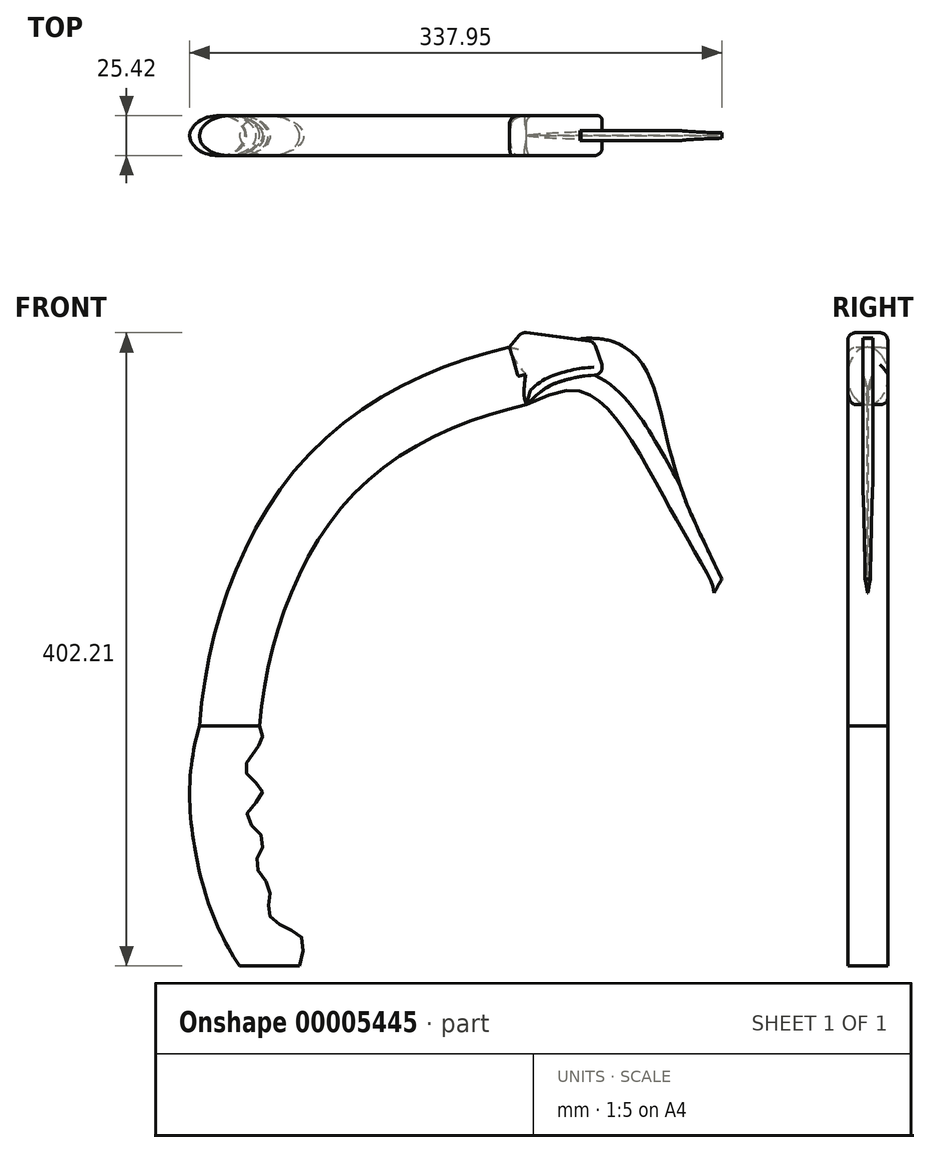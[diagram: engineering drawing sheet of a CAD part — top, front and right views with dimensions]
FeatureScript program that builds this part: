
annotation { "Feature Type Name" : "Feature", "Feature Type Description" : "" }
export const myFeature = defineFeature(function(context is Context, id is Id, definition is map)
    precondition{}
    {
        {
            var Q0;
            Q0=qCreatedBy(makeId("Top.planeOp"),FACE);
            var sketch = newSketch(context, id + "F0", { "sketchPlane" : qUnion([Q0])});
            skEllipse(sketch, "E0", {"center": v(0, 0) * mm, "majorRadius": 19.05 * mm, "minorRadius": 12.7 * mm, "majorAxis": v(-1, 0.02)});
            skLineSegment(sketch, "E1", {"start": v(0, 0) * mm, "end": v(-19.04, 0) * mm, "construction": true});
            skLineSegment(sketch, "E2", {"start": v(0, 0) * mm, "end": v(19.04, 0) * mm, "construction": true});
            skSolve(sketch);
        }
        {
            var Q0;
            Q0=qCreatedBy(makeId("Top.planeOp"),FACE);
            cPlane(context, id + "F1", {"entities" : qUnion([Q0]), "cplaneType" : CPlaneType.OFFSET, "offset" : 152.4 * mm, "width" : 152.4 * mm, "height" : 152.4 * mm});
        }
        {
            var Q0;
            Q0=qCreatedBy(id+"F1.planeOp",FACE);
            var sketch = newSketch(context, id + "F2", { "sketchPlane" : qUnion([Q0])});
            skEllipse(sketch, "E3", {"center": v(-25.4, 0) * mm, "majorRadius": 19.05 * mm, "minorRadius": 12.7 * mm, "majorAxis": v(-1, -0.03)});
            skLineSegment(sketch, "E4", {"start": v(-25.4, 0) * mm, "end": v(-44.44, 0) * mm, "construction": true});
            skLineSegment(sketch, "E5", {"start": v(-25.4, 0) * mm, "end": v(-6.36, 0) * mm, "construction": true});
            skSolve(sketch);
        }
        {
            var Q0;
            Q0=qCreatedBy(makeId("Front.planeOp"),FACE);
            var sketch = newSketch(context, id + "F3", { "sketchPlane" : qUnion([Q0])});
            skFitSpline(sketch, "E6", {"points": [v(-19.04, 0) * mm, v(-47.63, 75.12) * mm, v(-44.44, 152.4) * mm], "startDerivative": vector(-95.5, 140.87) * mm, "endDerivative": vector(49.4, 163.1) * mm});
            skFitSpline(sketch, "E7", {"points": [v(19.04, 0) * mm, v(19.67, 19.02) * mm, v(0, 31.78) * mm, v(0, 48.7) * mm, v(-8.8, 65.02) * mm, v(-3.57, 79.8) * mm, v(-14.65, 95.18) * mm, v(-4.5, 110.26) * mm, v(-15.27, 123.8) * mm, v(-6.96, 139.81) * mm, v(-6.36, 152.4) * mm], "startDerivative": vector(53.2, 280.33) * mm, "endDerivative": vector(-108.4, 99.62) * mm});
            skSolve(sketch);
        }
        {
            var Q0;
            Q0=makeQuery(id+"F2.imprint","IMPRINT",FACE,{"disambiguationData":[TD([[makeQuery(id+"F2.imprint","IMPRINT",EDGE,{"derivedFrom":sQuery(id+"F2.wireOp",EDGE,"E3")}),1.0]])]});
            var Q1;
            Q1=makeQuery(id+"F0.imprint","IMPRINT",FACE,{"disambiguationData":[TD([[makeQuery(id+"F0.imprint","IMPRINT",EDGE,{"derivedFrom":sQuery(id+"F0.wireOp",EDGE,"E0")}),1.0]])]});
            var Q2;
            Q2=sQuery(id+"F3.wireOp",EDGE,"E6");
            var Q3;
            Q3=sQuery(id+"F3.wireOp",EDGE,"E7");
            loft(context, id + "F4", {"addGuides" : true, "sheetProfilesArray" : [{ "sheetProfileEntities" : qUnion([Q0]) }, { "sheetProfileEntities" : qUnion([Q1]) }], "guidesArray" : [{ "guideEntities" : qUnion([Q2]), "guideDerivativeType" : LoftGuideDerivativeType.DEFAULT, "guideDerivativeMagnitude" : 1 }, { "guideEntities" : qUnion([Q3]), "guideDerivativeType" : LoftGuideDerivativeType.DEFAULT, "guideDerivativeMagnitude" : 1 }]});
        }
        {
            var Q0;
            Q0=qCreatedBy(makeId("Front.planeOp"),FACE);
            var sketch = newSketch(context, id + "F5", { "sketchPlane" : qUnion([Q0])});
            skFitSpline(sketch, "E8", {"points": [v(-44.44, 152.4) * mm, v(23.01, 322.86) * mm, v(152.4, 392.96) * mm], "startDerivative": vector(23.52, 350.72) * mm, "endDerivative": vector(281.64, 63.12) * mm});
            skLineSegment(sketch, "E9", {"start": v(0, 0) * mm, "end": v(152.4, 0) * mm});
            skSolve(sketch);
        }
        {
            var Q0;
            Q0=makeQuery(id+"F4.opLoft","CAP_FACE",FACE,{"disambiguationData":[OSD([makeQuery(id+"F2.imprint","IMPRINT",FACE,{"disambiguationData":[TD([[makeQuery(id+"F2.imprint","IMPRINT",EDGE,{"derivedFrom":sQuery(id+"F2.wireOp",EDGE,"E3")}),1.0]])]})])],"isStart":true});
            var Q1;
            Q1=sQuery(id+"F5.wireOp",EDGE,"E8");
            sweep(context, id + "F6", {"operationType" : NewBodyOperationType.ADD, "profiles" : qUnion([Q0]), "path" : qUnion([Q1])});
        }
        {
            var Q0;
            Q0=qCreatedBy(makeId("Front.planeOp"),FACE);
            var sketch = newSketch(context, id + "F7", { "sketchPlane" : qUnion([Q0])});
            skFitSpline(sketch, "E10", {"points": [v(197.62, 398.4) * mm, v(236.29, 382.89) * mm, v(251.85, 337) * mm, v(261.11, 304.05) * mm, v(287.2, 245.73) * mm], "startDerivative": vector(230.2, 21.85) * mm, "endDerivative": vector(193.51, -403.47) * mm});
            skFitSpline(sketch, "E11", {"points": [v(163.2, 356.44) * mm, v(207.45, 360.06) * mm, v(227.94, 336.77) * mm, v(252.58, 293.78) * mm, v(267.92, 266.78) * mm, v(280.46, 244.2) * mm, v(282.32, 236.95) * mm], "startDerivative": vector(375.19, 192.04) * mm, "endDerivative": vector(9.77, -124.3) * mm});
            skLineSegment(sketch, "E12", {"start": v(287.2, 245.73) * mm, "end": v(282.32, 236.95) * mm});
            skLineSegment(sketch, "E13", {"start": v(197.62, 398.4) * mm, "end": v(163.2, 356.44) * mm});
            skSolve(sketch);
        }
        {
            var Q0;
            Q0=makeQuery(id+"F7.imprint","IMPRINT",FACE,{"disambiguationData":[TD([[makeQuery(id+"F7.imprint","IMPRINT",EDGE,{"derivedFrom":sQuery(id+"F7.wireOp",EDGE,"E10")}),-1.0]])]});
            extrude(context, id + "F8", {"entities" : qUnion([Q0]), "operationType" : NewBodyOperationType.ADD, "endBound" : BoundingType.SYMMETRIC, "depth" : 6.35 * mm});
        }
        {
            var Q0;
            Q0=qCreatedBy(makeId("Front.planeOp"),FACE);
            var sketch = newSketch(context, id + "F9", { "sketchPlane" : qUnion([Q0])});
            skLineSegment(sketch, "E14", {"start": v(163.2, 356.44) * mm, "end": v(152.4, 392.96) * mm});
            skLineSegment(sketch, "E15", {"start": v(205.84, 396.62) * mm, "end": v(213.34, 375.23) * mm});
            skLineSegment(sketch, "E16", {"start": v(152.4, 392.96) * mm, "end": v(160.2, 402.53) * mm});
            skLineSegment(sketch, "E17", {"start": v(160.2, 402.53) * mm, "end": v(205.84, 396.62) * mm});
            skFitSpline(sketch, "E18", {"points": [v(213.34, 375.23) * mm, v(184.24, 371.01) * mm, v(163.2, 356.44) * mm], "startDerivative": vector(-74.46, 3.6) * mm, "endDerivative": vector(-65.74, -66.24) * mm});
            skSolve(sketch);
        }
        {
            var Q0;
            Q0=makeQuery(id+"F9.imprint","IMPRINT",FACE,{"disambiguationData":[TD([[makeQuery(id+"F9.imprint","IMPRINT",EDGE,{"derivedFrom":sQuery(id+"F9.wireOp",EDGE,"E14")}),-1.0]])]});
            extrude(context, id + "F10", {"entities" : qUnion([Q0]), "operationType" : NewBodyOperationType.ADD, "endBound" : BoundingType.SYMMETRIC, "depth" : 25.4 * mm});
        }
        {
            var Q0;
            Q0=makeQuery(id+"F10.opExtrude","CAP_EDGE",EDGE,{"disambiguationData":[OSD([sQuery(id+"F9.wireOp",EDGE,"E18")])],"isStart":false});
            var Q1;
            Q1=makeQuery(id+"F10.opExtrude","CAP_EDGE",EDGE,{"disambiguationData":[OSD([sQuery(id+"F9.wireOp",EDGE,"E15")])],"isStart":false});
            var Q2;
            Q2=makeQuery(id+"F10.opExtrude","CAP_EDGE",EDGE,{"disambiguationData":[OSD([sQuery(id+"F9.wireOp",EDGE,"E17")])],"isStart":false});
            var Q3;
            Q3=makeQuery(id+"F10.opExtrude","CAP_EDGE",EDGE,{"disambiguationData":[OSD([sQuery(id+"F9.wireOp",EDGE,"E16")])],"isStart":false});
            var Q4;
            {var subQ0=sQuery(id+"F9.wireOp",EDGE,"E14");var subQ1=sQuery(id+"F9.wireOp",EDGE,"E18");Q4=makeQuery(id+"F10.boolean.opBoolean","SPLIT",EDGE,{"disambiguationData":[TD([makeQuery(id+"F10.opExtrude","SWEPT_FACE",FACE,{"disambiguationData":[OSD([subQ1])]})])],"derivedFrom":makeQuery(id+"F10.opExtrude","CAP_EDGE",EDGE,{"disambiguationData":[OSD([subQ0])],"isStart":false})});}
            var Q5;
            Q5=makeQuery(id+"F10.opExtrude","SWEPT_EDGE",EDGE,{"disambiguationData":[OSD([sQuery(id+"F9.wireOp",EDGE,"E16"),sQuery(id+"F9.wireOp",EDGE,"E17")])]});
            var Q6;
            Q6=makeQuery(id+"F10.opExtrude","CAP_EDGE",EDGE,{"disambiguationData":[OSD([sQuery(id+"F9.wireOp",EDGE,"E16")])],"isStart":true});
            var Q7;
            {var subQ0=sQuery(id+"F9.wireOp",EDGE,"E14");var subQ1=sQuery(id+"F9.wireOp",EDGE,"E16");Q7=makeQuery(id+"F10.boolean.opBoolean","SPLIT",EDGE,{"disambiguationData":[TD([makeQuery(id+"F10.opExtrude","SWEPT_FACE",FACE,{"disambiguationData":[OSD([subQ1])]})])],"derivedFrom":makeQuery(id+"F10.opExtrude","CAP_EDGE",EDGE,{"disambiguationData":[OSD([subQ0])],"isStart":true})});}
            var Q8;
            Q8=makeQuery(id+"F10.opExtrude","CAP_EDGE",EDGE,{"disambiguationData":[OSD([sQuery(id+"F9.wireOp",EDGE,"E17")])],"isStart":true});
            var Q9;
            Q9=makeQuery(id+"F10.opExtrude","CAP_EDGE",EDGE,{"disambiguationData":[OSD([sQuery(id+"F9.wireOp",EDGE,"E15")])],"isStart":true});
            var Q10;
            {var subQ0=sQuery(id+"F9.wireOp",EDGE,"E15");var subQ1=sQuery(id+"F9.wireOp",EDGE,"E18");Q10=makeQuery(id+"F10.boolean.opBoolean","SPLIT",EDGE,{"disambiguationData":[TD([makeQuery(id+"F8.opExtrude","CAP_FACE",FACE,{"disambiguationData":[OSD([sQuery(id+"F7.wireOp",EDGE,"E10"),sQuery(id+"F7.wireOp",EDGE,"E11"),sQuery(id+"F7.wireOp",EDGE,"E12"),sQuery(id+"F7.wireOp",EDGE,"E13")])],"isStart":true})])],"derivedFrom":makeQuery(id+"F10.opExtrude","SWEPT_EDGE",EDGE,{"disambiguationData":[OSD([subQ0,subQ1])]})});}
            var Q11;
            {var subQ0=sQuery(id+"F9.wireOp",EDGE,"E15");var subQ1=sQuery(id+"F9.wireOp",EDGE,"E18");Q11=makeQuery(id+"F10.boolean.opBoolean","SPLIT",EDGE,{"disambiguationData":[TD([makeQuery(id+"F8.opExtrude","CAP_FACE",FACE,{"disambiguationData":[OSD([sQuery(id+"F7.wireOp",EDGE,"E10"),sQuery(id+"F7.wireOp",EDGE,"E11"),sQuery(id+"F7.wireOp",EDGE,"E12"),sQuery(id+"F7.wireOp",EDGE,"E13")])],"isStart":false})])],"derivedFrom":makeQuery(id+"F10.opExtrude","SWEPT_EDGE",EDGE,{"disambiguationData":[OSD([subQ0,subQ1])]})});}
            var Q12;
            {var subQ0=sQuery(id+"F9.wireOp",EDGE,"E15");var subQ1=sQuery(id+"F9.wireOp",EDGE,"E17");Q12=makeQuery(id+"F10.boolean.opBoolean","SPLIT",EDGE,{"disambiguationData":[TD([makeQuery(id+"F8.opExtrude","CAP_FACE",FACE,{"disambiguationData":[OSD([sQuery(id+"F7.wireOp",EDGE,"E10"),sQuery(id+"F7.wireOp",EDGE,"E11"),sQuery(id+"F7.wireOp",EDGE,"E12"),sQuery(id+"F7.wireOp",EDGE,"E13")])],"isStart":false})])],"derivedFrom":makeQuery(id+"F10.opExtrude","SWEPT_EDGE",EDGE,{"disambiguationData":[OSD([subQ0,subQ1])]})});}
            var Q13;
            {var subQ0=sQuery(id+"F9.wireOp",EDGE,"E15");var subQ1=sQuery(id+"F9.wireOp",EDGE,"E17");Q13=makeQuery(id+"F10.boolean.opBoolean","SPLIT",EDGE,{"disambiguationData":[TD([makeQuery(id+"F8.opExtrude","CAP_FACE",FACE,{"disambiguationData":[OSD([sQuery(id+"F7.wireOp",EDGE,"E10"),sQuery(id+"F7.wireOp",EDGE,"E11"),sQuery(id+"F7.wireOp",EDGE,"E12"),sQuery(id+"F7.wireOp",EDGE,"E13")])],"isStart":true})])],"derivedFrom":makeQuery(id+"F10.opExtrude","SWEPT_EDGE",EDGE,{"disambiguationData":[OSD([subQ0,subQ1])]})});}
            fillet(context, id + "F11", {"entities" : qUnion([Q0, Q1, Q2, Q3, Q4, Q5, Q6, Q7, Q8, Q9, Q10, Q11, Q12, Q13]), "radius" : 5.08 * mm, "tangentPropagation" : true, "allowEdgeOverflow" : false});
        }
        {
            var Q0;
            Q0=makeQuery(id+"F8.opExtrude","CAP_EDGE",EDGE,{"disambiguationData":[OSD([sQuery(id+"F7.wireOp",EDGE,"E11")])],"isStart":true});
            var Q1;
            Q1=makeQuery(id+"F8.opExtrude","CAP_EDGE",EDGE,{"disambiguationData":[OSD([sQuery(id+"F7.wireOp",EDGE,"E11")])],"isStart":false});
            chamfer(context, id + "F12", {"entities" : qUnion([Q0, Q1]), "chamferType" : ChamferType.TWO_OFFSETS, "width1" : 3.05 * mm, "oppositeDirection" : false, "width2" : 12.7 * mm, "tangentPropagation" : true});
        }
    });
